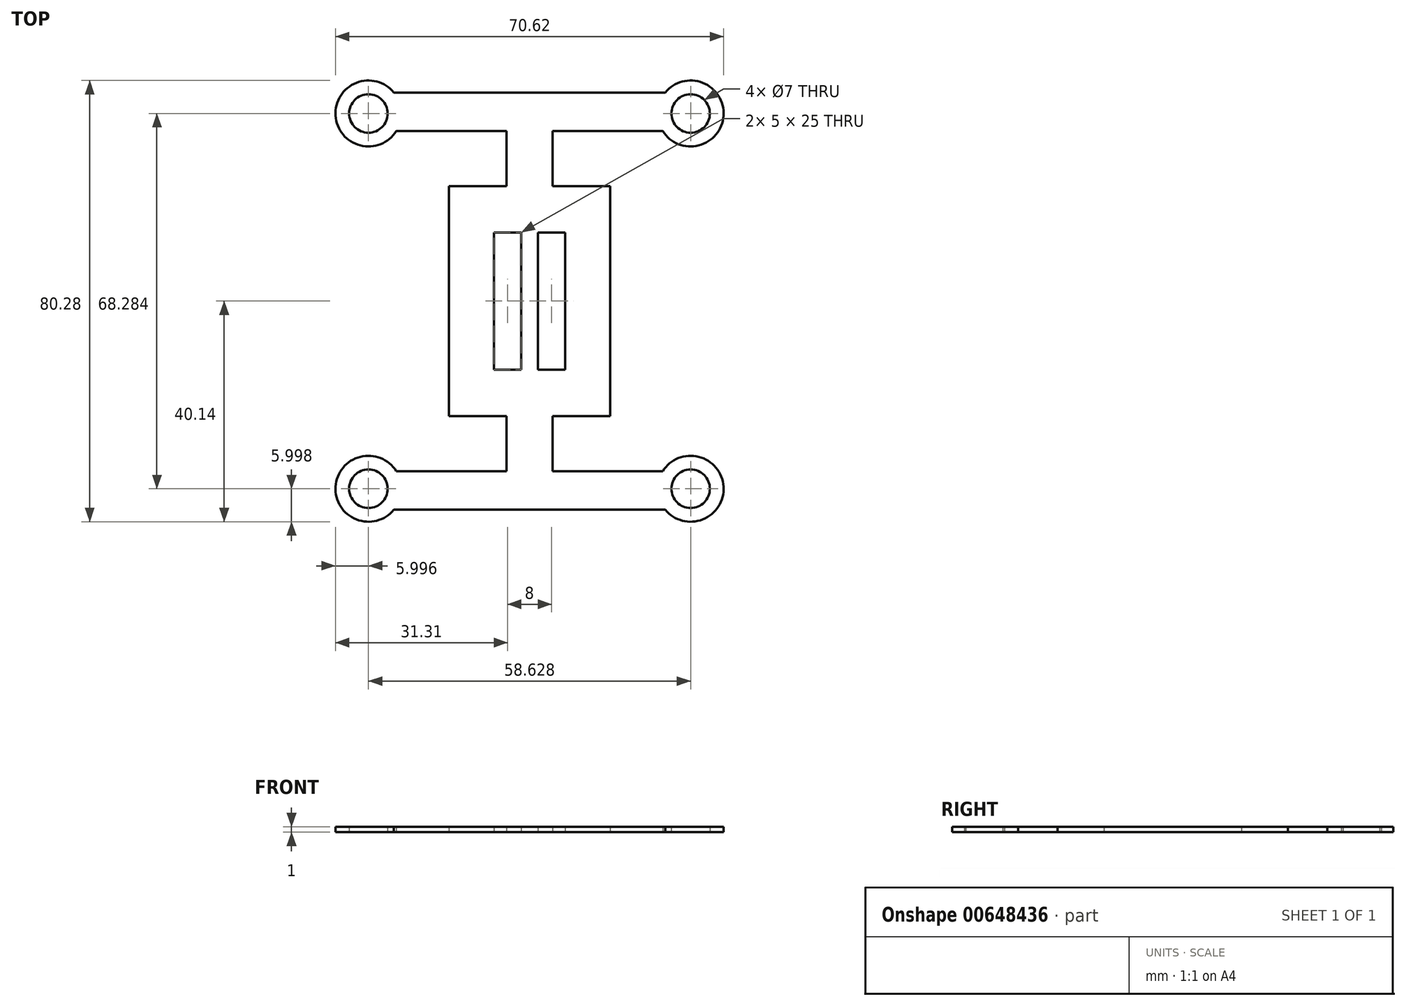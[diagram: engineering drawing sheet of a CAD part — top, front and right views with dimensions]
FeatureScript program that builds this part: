
annotation { "Feature Type Name" : "Feature", "Feature Type Description" : "" }
export const myFeature = defineFeature(function(context is Context, id is Id, definition is map)
    precondition{}
    {
        {
            var Q0;
            Q0=qCreatedBy(makeId("Top.planeOp"),FACE);
            var sketch = newSketch(context, id + "F0", { "sketchPlane" : qUnion([Q0])});
            skLineSegment(sketch, "E0.bottom", {"start": v(-29.31, 34.14) * mm, "end": v(29.31, 34.14) * mm, "construction": true});
            skLineSegment(sketch, "E0.top", {"start": v(-29.31, -34.14) * mm, "end": v(29.31, -34.14) * mm, "construction": true});
            skLineSegment(sketch, "E0.left", {"start": v(-29.31, 34.14) * mm, "end": v(-29.31, -34.14) * mm, "construction": true});
            skLineSegment(sketch, "E0.right", {"start": v(29.31, 34.14) * mm, "end": v(29.31, -34.14) * mm, "construction": true});
            skPoint(sketch, "E0.middle", {"position": v(0, 0) * mm});
            skLineSegment(sketch, "E1", {"start": v(0, 49.78) * mm, "end": v(0, 0) * mm, "construction": true});
            skLineSegment(sketch, "E2", {"start": v(0, 0) * mm, "end": v(52.54, 0) * mm, "construction": true});
            skCircle(sketch, "E3", {"center": v(29.31, 34.14) * mm, "radius": 3.5 * mm});
            skCircle(sketch, "E4", {"center": v(29.31, 34.14) * mm, "radius": 6 * mm});
            skLineSegment(sketch, "E5", {"start": v(0, 37.95) * mm, "end": v(24.67, 37.95) * mm});
            skLineSegment(sketch, "E6", {"start": v(24.24, 30.95) * mm, "end": v(4.22, 30.95) * mm});
            skLineSegment(sketch, "E7", {"start": v(4.22, 30.95) * mm, "end": v(4.22, 20.95) * mm});
            skLineSegment(sketch, "E8", {"start": v(4.22, 20.95) * mm, "end": v(14.65, 20.95) * mm});
            skLineSegment(sketch, "E9", {"start": v(14.65, 20.95) * mm, "end": v(14.65, 0) * mm});
            skLineSegment(sketch, "E10.MirrorCS", {"start": v(-14.65, 20.95) * mm, "end": v(-14.65, 0) * mm});
            skLineSegment(sketch, "E11.MirrorCS", {"start": v(-4.22, 20.95) * mm, "end": v(-14.65, 20.95) * mm});
            skLineSegment(sketch, "E12.MirrorCS", {"start": v(-4.22, 30.95) * mm, "end": v(-4.22, 20.95) * mm});
            skLineSegment(sketch, "E13.MirrorCS", {"start": v(0, 37.95) * mm, "end": v(-24.67, 37.95) * mm});
            skLineSegment(sketch, "E14.MirrorCS", {"start": v(-24.24, 30.95) * mm, "end": v(-4.22, 30.95) * mm});
            skCircle(sketch, "E15.MirrorC", {"center": v(-29.31, 34.14) * mm, "radius": 6 * mm});
            skCircle(sketch, "E16.MirrorC", {"center": v(-29.31, 34.14) * mm, "radius": 3.5 * mm});
            skLineSegment(sketch, "E17.MirrorCS", {"start": v(0, -37.95) * mm, "end": v(-24.67, -37.95) * mm});
            skCircle(sketch, "E18.MirrorC", {"center": v(29.31, -34.14) * mm, "radius": 3.5 * mm});
            skLineSegment(sketch, "E19.MirrorCS", {"start": v(0, -37.95) * mm, "end": v(24.67, -37.95) * mm});
            skLineSegment(sketch, "E20.MirrorCS", {"start": v(29.31, -34.14) * mm, "end": v(29.31, 34.14) * mm, "construction": true});
            skLineSegment(sketch, "E21.MirrorCS", {"start": v(14.65, -20.95) * mm, "end": v(14.65, 0) * mm});
            skLineSegment(sketch, "E22.MirrorCS", {"start": v(4.22, -20.95) * mm, "end": v(14.65, -20.95) * mm});
            skLineSegment(sketch, "E23.MirrorCS", {"start": v(24.24, -30.95) * mm, "end": v(4.22, -30.95) * mm});
            skCircle(sketch, "E24.MirrorC", {"center": v(29.31, -34.14) * mm, "radius": 6 * mm});
            skLineSegment(sketch, "E25.MirrorCS", {"start": v(4.22, -30.95) * mm, "end": v(4.22, -20.95) * mm});
            skLineSegment(sketch, "E26.MirrorCS", {"start": v(-14.65, -20.95) * mm, "end": v(-14.65, 0) * mm});
            skLineSegment(sketch, "E27.MirrorCS", {"start": v(-24.24, -30.95) * mm, "end": v(-4.22, -30.95) * mm});
            skCircle(sketch, "E28.MirrorC", {"center": v(-29.31, -34.14) * mm, "radius": 3.5 * mm});
            skCircle(sketch, "E29.MirrorC", {"center": v(-29.31, -34.14) * mm, "radius": 6 * mm});
            skLineSegment(sketch, "E30.MirrorCS", {"start": v(-4.22, -20.95) * mm, "end": v(-14.65, -20.95) * mm});
            skLineSegment(sketch, "E31.MirrorCS", {"start": v(-4.22, -30.95) * mm, "end": v(-4.22, -20.95) * mm});
            skLineSegment(sketch, "E32.bottom", {"start": v(-6.5, 12.5) * mm, "end": v(-1.5, 12.5) * mm});
            skLineSegment(sketch, "E32.top", {"start": v(-6.5, -12.5) * mm, "end": v(-1.5, -12.5) * mm});
            skLineSegment(sketch, "E32.left", {"start": v(-6.5, 12.5) * mm, "end": v(-6.5, -12.5) * mm});
            skLineSegment(sketch, "E32.right", {"start": v(-1.5, 12.5) * mm, "end": v(-1.5, -12.5) * mm});
            skPoint(sketch, "E32.middle", {"position": v(-4, 0) * mm});
            skLineSegment(sketch, "E33.MirrorCS", {"start": v(6.5, 12.5) * mm, "end": v(6.5, -12.5) * mm});
            skPoint(sketch, "E34.MirrorP", {"position": v(4, 0) * mm});
            skLineSegment(sketch, "E35.MirrorCS", {"start": v(6.5, -12.5) * mm, "end": v(1.5, -12.5) * mm});
            skLineSegment(sketch, "E36.MirrorCS", {"start": v(1.5, 12.5) * mm, "end": v(1.5, -12.5) * mm});
            skLineSegment(sketch, "E37.MirrorCS", {"start": v(6.5, 12.5) * mm, "end": v(1.5, 12.5) * mm});
            skSolve(sketch);
        }
        {
            var Q0;
            Q0=qSketchRegion(id+"F0",true);
            extrude(context, id + "F1", {"entities" : qUnion([Q0]), "depth" : 1 * mm, "offsetDistance" : 25 * mm});
        }
    });
